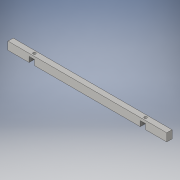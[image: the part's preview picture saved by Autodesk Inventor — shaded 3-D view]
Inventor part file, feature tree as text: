
AUTODESK INVENTOR PART (.ipt)
format: ipt  version: 2016 (Build 200138000, 138)  size: 117,248 bytes
history: native  units: in
note: dims shown in document units (in); Inventor stores cm internally (conversion verified against a paired STEP export)
features: sketch x3, extrude x2, hole x1
ambient origin geometry x8: Origin, YZ Plane, XZ Plane, XY Plane, X Axis, Y Axis, Z Axis, Center Point
bodies: Solid1 (feature_tree)
feature tree (6):
  extrude  "Extrusion1"  Depth=0.5in
  extrude  "Extrusion2"  Depth=0.5in
  hole  "Hole1"  [1 undecoded]
  sketch  "Sketch1"  dims[d0=15.0in d1=0.5in]
  sketch  "Sketch2"  dims[d2=0.75in d3=0.0in d4=0.5in]
  sketch  "Sketch3"  dims[d5=0.5in d6=2.0in d7=0.5in d8=0.5in d9=13.0in d10=0.5in d11=0.0in d12=0.25in d13=2.25in d15=0.25in d16=0.25in d17=12.75in d18=0.25in d19=0.75in d20=0.375in d21=0.25in d22=0.5635in d23=1.0in d24=0.8108in]
note: 1 required parameter value undecoded (feature->parameter linkage not recoverable at this tier; creation-order binding heuristic only, values carry confidence <= 0.55)
